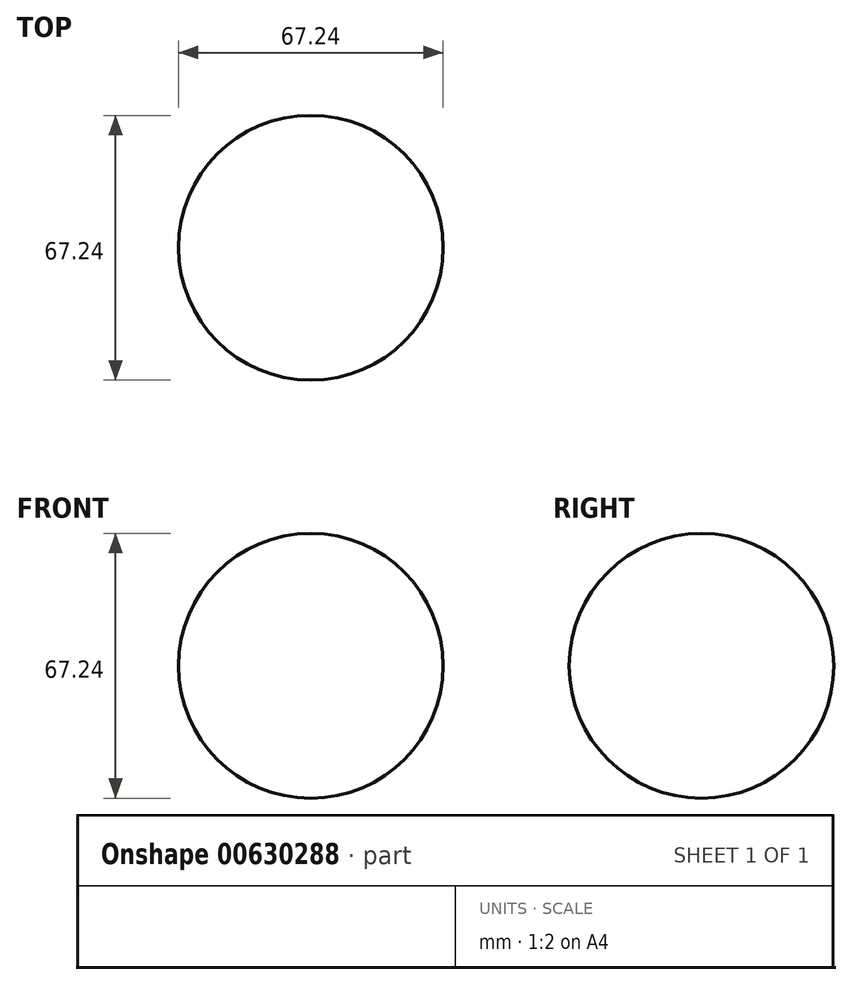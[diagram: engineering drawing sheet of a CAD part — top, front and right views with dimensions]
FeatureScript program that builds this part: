
annotation { "Feature Type Name" : "Feature", "Feature Type Description" : "" }
export const myFeature = defineFeature(function(context is Context, id is Id, definition is map)
    precondition{}
    {
        {
            var Q0;
            Q0=qCreatedBy(makeId("Front.planeOp"),FACE);
            var sketch = newSketch(context, id + "F0", { "sketchPlane" : qUnion([Q0])});
            skArc(sketch, "E0", {"start": v(0, 33.62) * mm, "mid": v(-33.62, 0) * mm, "end": v(0, -33.62) * mm});
            skLineSegment(sketch, "E1", {"start": v(0, 33.62) * mm, "end": v(0, -33.62) * mm});
            skSolve(sketch);
        }
        {
            var Q0;
            Q0=makeQuery(id+"F0.imprint","IMPRINT",FACE,{"disambiguationData":[TD([[makeQuery(id+"F0.imprint","IMPRINT",EDGE,{"derivedFrom":sQuery(id+"F0.wireOp",EDGE,"E0")}),1.0]])]});
            var Q1;
            Q1=sQuery(id+"F0.wireOp",EDGE,"E1");
            revolve(context, id + "F1", {"entities" : qUnion([Q0]), "axis" : qUnion([Q1]), "revolveType" : RevolveType.FULL});
        }
    });
